# Revit family: Heater-QMark-Thermazone_Series
name_source: partatom
category: Mechanical Equipment
units: mm (PartAtom-declared; Revit-internal decimal feet)

## family parameters
Classification = None
Cut with Voids When Loaded = No
Host = Face
OmniClass Number = 23.75.70.17.17
OmniClass Title = Radiation Panels
Part Type = Normal
Room Calculation Point = No
Round Connector Dimension = Use Diameter
Shared = No

## types (75) — shared parameters
Assembly Code = D3060300
C_ Thermazone Series 1' = Yes
Default Elevation = 6' - 0"
Depth = 1' - 0"
Description = Infrared Heaters for Industrial/Commercial/Residential
Frequency = 60 Hz
Height = 0' - 5 1/2"
Infrared Material = Paint - QMark - Powder Coated Black (BK)
Instruction Sheet Link = https://www.marleymep.com
Keynote = 15500
Manufacturer = Marley® Engineered Products
Number of Poles = 1
Power Factor = 1
Product Documentation Link = https://www.marleymep.com
Product Name = Thermazone Series - Commercial/Residential Infrared Heater
Product Page URL = https://www.marleymep.com
URL = https://www.marleymep.com
Version = 2020 - v1.0a

## per-type parameters (varying)
| type | Amps | C_ Thermazone Series 2' | C_ Thermazone Series 4' | Length | Phase | Total Heating Capacity | Voltage | Watts |
| QR-STS-U12-0871B | 7 A | No | No | 1' - 0" | 1 | 2972.0 Btu/h | 120 V | 871 W |
| QR-STS-U12-1081B | 9 A | No | No | 1' - 0" | 1 | 3688.0 Btu/h | 120 V | 1081 W |
| QR-STS-U12-1111B | 9 A | No | No | 1' - 0" | 1 | 3790.0 Btu/h | 120 V | 1111 W |
| QR-STS-U12-1681B | 14 A | No | No | 1' - 0" | 1 | 5735.0 Btu/h | 120 V | 1681 W |
| QR-STS-U12-1077V | 5 A | No | No | 1' - 0" | 1 | 3674.0 Btu/h | 208 V | 1077 W |
| QR-STS-U12-1436V | 6 A | No | No | 1' - 0" | 1 | 4890.0 Btu/h | 240 V | 1436 W |
| QR-STS-U24-1015V | 4 A | Yes | No | 2' - 0" | 1 | 3463.0 Btu/h | 240 V | 1015 W |
| QR-STS-U24-1316B | 11 A | Yes | No | 2' - 0" | 1 | 4490.0 Btu/h | 120 V | 1316 W |
| QR-STS-U24-1297V | 5 A | Yes | No | 2' - 0" | 1 | 4425.0 Btu/h | 240 V | 1297 W |
| QR-STS-U24-1659B | 14 A | Yes | No | 2' - 0" | 1 | 5660.0 Btu/h | 120 V | 1659 W |
| QR-STS-U24-1276V | 6 A | Yes | No | 2' - 0" | 1 | 4353.0 Btu/h | 208 V | 1276 W |
| QR-STS-U24-1701V | 7 A | Yes | No | 2' - 0" | 1 | 5804.0 Btu/h | 240 V | 1701 W |
| QR-STS-U24-2192B | 18 A | Yes | No | 2' - 0" | 1 | 7479.0 Btu/h | 120 V | 2192 W |
| QR-STS-U24-1501V | 7 A | Yes | No | 2' - 0" | 1 | 5121.0 Btu/h | 208 V | 1501 W |
| QR-STS-U24-2001V | 8 A | Yes | No | 2' - 0" | 1 | 6827.0 Btu/h | 240 V | 2001 W |
| QR-STS-U24-1982N | 7 A | Yes | No | 2' - 0" | 1 | 6762.0 Btu/h | 277 V | 1982 W |
| QR-STS-U24-2060I | 6 A | Yes | No | 2' - 0" | 1 | 7029.0 Btu/h | 347 V | 2060 W |
| QR-STS-U24-2222B | 19 A | Yes | No | 2' - 0" | 1 | 7581.0 Btu/h | 120 V | 2222 W |
| QR-STS-U24-1821V | 9 A | Yes | No | 2' - 0" | 1 | 6213.0 Btu/h | 208 V | 1821 W |
| QR-STS-U24-2428V | 10 A | Yes | No | 2' - 0" | 1 | 8284.0 Btu/h | 240 V | 2428 W |
| QR-STS-U24-2388N | 9 A | Yes | No | 2' - 0" | 1 | 8148.0 Btu/h | 277 V | 2388 W |
| QR-STS-U24-2488I | 7 A | Yes | No | 2' - 0" | 1 | 8489.0 Btu/h | 347 V | 2488 W |
| QR-STS-U24-3363B | 28 A | Yes | No | 2' - 0" | 1 | 11475.0 Btu/h | 120 V | 3363 W |
| QR-STS-U24-2429V | 12 A | Yes | No | 2' - 0" | 1 | 8288.0 Btu/h | 208 V | 2429 W |
| QR-STS-U24-3239V | 14 A | Yes | No | 2' - 0" | 1 | 11051.0 Btu/h | 240 V | 3239 W |
| QR-STS-U24-3008N | 10 A | Yes | No | 2' - 0" | 1 | 10263.0 Btu/h | 277 V | 3008 W |
| QR-STS-U24-3176I | 9 A | Yes | No | 2' - 0" | 1 | 10836.0 Btu/h | 347 V | 3176 W |
| QR-STS-U24-1496P | 4 A | Yes | No | 2' - 0" | 3 | 5104.0 Btu/h | 208 V | 1496 W |
| QR-STS-U24-1992P | 5 A | Yes | No | 2' - 0" | 3 | 6796.0 Btu/h | 240 V | 1992 W |
| QR-STS-U24-1834P | 5 A | Yes | No | 2' - 0" | 3 | 6257.0 Btu/h | 208 V | 1834 W |
| QR-STS-U24-2442P | 6 A | Yes | No | 2' - 0" | 3 | 8332.0 Btu/h | 240 V | 2442 W |
| QR-STS-U24-2284P | 6 A | Yes | No | 2' - 0" | 3 | 7793.0 Btu/h | 208 V | 2284 W |
| QR-STS-U24-3021P | 7 A | Yes | No | 2' - 0" | 3 | 10376.0 Btu/h | 240 V | 3041 W |
| QR-STS-U48-1523V | 7 A | Yes | Yes | 4' - 0" | 1 | 5196.0 Btu/h | 208 V | 1523 W |
| QR-STS-U48-2030V | 9 A | Yes | Yes | 4' - 0" | 1 | 6926.0 Btu/h | 240 V | 2030 W |
| QR-STS-U48-2014I | 6 A | Yes | Yes | 4' - 0" | 1 | 6872.0 Btu/h | 347 V | 2014 W |
| QR-STS-U48-2030T | 4 A | Yes | Yes | 4' - 0" | 1 | 6926.0 Btu/h | 480 V | 2030 W |
| QR-STS-U48-1946V | 9 A | Yes | Yes | 4' - 0" | 1 | 6640.0 Btu/h | 208 V | 1946 W |
| QR-STS-U48-2594V | 11 A | Yes | Yes | 4' - 0" | 1 | 8851.0 Btu/h | 240 V | 2594 W |
| QR-STS-U48-2502I | 7 A | Yes | Yes | 4' - 0" | 1 | 8537.0 Btu/h | 347 V | 2502 W |
| QR-STS-U48-2594T | 5 A | Yes | Yes | 4' - 0" | 1 | 8851.0 Btu/h | 480 V | 2594 W |
| QR-STS-U48-2552V | 12 A | Yes | Yes | 4' - 0" | 1 | 8707.0 Btu/h | 208 V | 2552 W |
| QR-STS-U48-3402V | 14 A | Yes | Yes | 4' - 0" | 1 | 11608.0 Btu/h | 240 V | 3402 W |
| QR-STS-U48-3206I | 9 A | Yes | Yes | 4' - 0" | 1 | 10939.0 Btu/h | 347 V | 3206 W |
| QR-STS-U48-3402T | 7 A | Yes | Yes | 4' - 0" | 1 | 11608.0 Btu/h | 480 V | 3402 W |
| QR-STS-U48-3002V | 15 A | Yes | Yes | 4' - 0" | 1 | 10243.0 Btu/h | 208 V | 3002 W |
| QR-STS-U48-4002V | 17 A | Yes | Yes | 4' - 0" | 1 | 13655.0 Btu/h | 240 V | 4002 W |
| QR-STS-U48-3964N | 14 A | Yes | Yes | 4' - 0" | 1 | 13525.0 Btu/h | 277 V | 3964 W |
| QR-STS-U48-4120I | 12 A | Yes | Yes | 4' - 0" | 1 | 14058.0 Btu/h | 347 V | 4120 W |
| QR-STS-U48-4002T | 8 A | Yes | Yes | 4' - 0" | 1 | 13655.0 Btu/h | 480 V | 4002 W |
| QR-STS-U48-4042Y | 7 A | Yes | Yes | 4' - 0" | 1 | 13791.0 Btu/h | 600 V | 4042 W |
| QR-STS-U48-3642V | 18 A | Yes | Yes | 4' - 0" | 1 | 12427.0 Btu/h | 208 V | 3642 W |
| QR-STS-U48-4856V | 20 A | Yes | Yes | 4' - 0" | 1 | 16569.0 Btu/h | 240 V | 4856 W |
| QR-STS-U48-4776N | 17 A | Yes | Yes | 4' - 0" | 1 | 16296.0 Btu/h | 277 V | 4776 W |
| QR-STS-U48-4976I | 14 A | Yes | Yes | 4' - 0" | 1 | 16978.0 Btu/h | 347 V | 4976 W |
| QR-STS-U48-4856T | 10 A | Yes | Yes | 4' - 0" | 1 | 16569.0 Btu/h | 480 V | 4856 W |
| QR-STS-U48-4878Y | 8 A | Yes | Yes | 4' - 0" | 1 | 16644.0 Btu/h | 600 V | 4878 W |
| QR-STS-U48-4859V | 23 A | Yes | Yes | 4' - 0" | 1 | 16579.0 Btu/h | 208 V | 4859 W |
| QR-STS-U48-6478V | 27 A | Yes | Yes | 4' - 0" | 1 | 22103.0 Btu/h | 240 V | 6478 W |
| QR-STS-U48-6056N | 22 A | Yes | Yes | 4' - 0" | 1 | 20663.0 Btu/h | 277 V | 6056 W |
| QR-STS-U48-6352I | 18 A | Yes | Yes | 4' - 0" | 1 | 21673.0 Btu/h | 347 V | 6352 W |
| QR-STS-U48-6478T | 14 A | Yes | Yes | 4' - 0" | 1 | 22103.0 Btu/h | 480 V | 6478 W |
| QR-STS-U48-6118Y | 10 A | Yes | Yes | 4' - 0" | 1 | 20875.0 Btu/h | 600 V | 6118 W |
| QR-STS-U48-2983P | 8 A | Yes | Yes | 4' - 0" | 3 | 10178.0 Btu/h | 208 V | 2983 W |
| QR-STS-U48-3971P | 10 A | Yes | Yes | 4' - 0" | 3 | 13549.0 Btu/h | 240 V | 3971 W |
| QR-STS-U48-3928U | 5 A | Yes | Yes | 4' - 0" | 3 | 13402.0 Btu/h | 480 V | 3928 W |
| QR-STS-U48-3963Z | 4 A | Yes | Yes | 4' - 0" | 3 | 13522.0 Btu/h | 600 V | 3963 W |
| QR-STS-U48-3601P | 10 A | Yes | Yes | 4' - 0" | 3 | 12287.0 Btu/h | 208 V | 3601 W |
| QR-STS-U48-4794P | 12 A | Yes | Yes | 4' - 0" | 3 | 16357.0 Btu/h | 240 V | 4794 W |
| QR-STS-U48-4838U | 6 A | Yes | Yes | 4' - 0" | 3 | 16507.0 Btu/h | 480 V | 4838 W |
| QR-STS-U48-4797Z | 5 A | Yes | Yes | 4' - 0" | 3 | 16369.0 Btu/h | 600 V | 4797 W |
| QR-STS-U48-4472P | 12 A | Yes | Yes | 4' - 0" | 3 | 15259.0 Btu/h | 208 V | 4472 W |
| QR-STS-U48-5954P | 14 A | Yes | Yes | 4' - 0" | 3 | 20315.0 Btu/h | 240 V | 5954 W |
| QR-STS-U48-6060U | 7 A | Yes | Yes | 4' - 0" | 3 | 20677.0 Btu/h | 480 V | 6060 W |
| QR-STS-U48-5982Z | 6 A | Yes | Yes | 4' - 0" | 3 | 20411.0 Btu/h | 600 V | 5982 W |

note: column(s) folded — value = type name in every type: Model

## geometry (parser evidence)
native form markers: Sweep x13
no freeform markers — native parametric forms only
